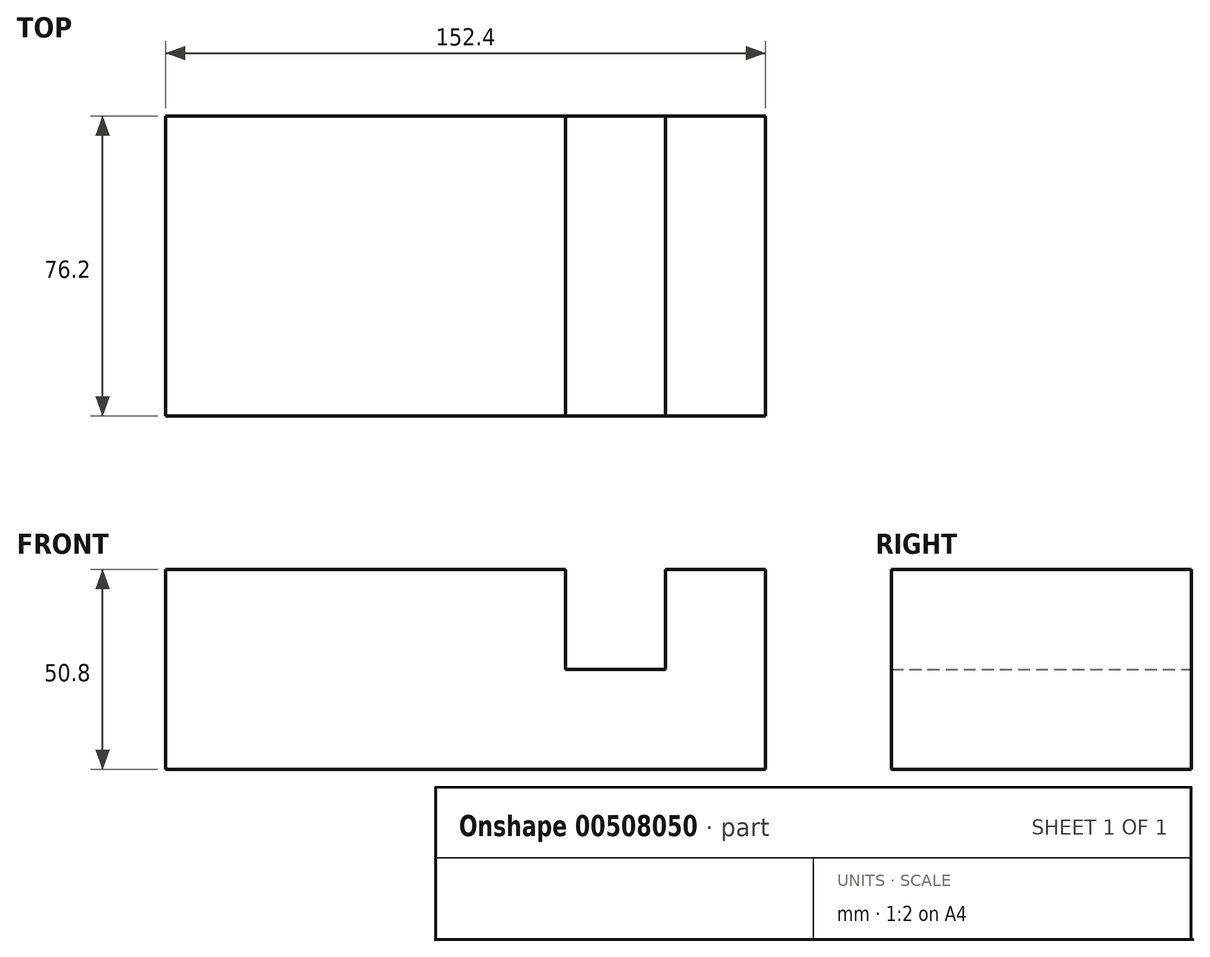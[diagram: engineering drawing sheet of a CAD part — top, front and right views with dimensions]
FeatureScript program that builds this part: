
annotation { "Feature Type Name" : "Feature", "Feature Type Description" : "" }
export const myFeature = defineFeature(function(context is Context, id is Id, definition is map)
    precondition{}
    {
        {
            var Q0;
            Q0=qCreatedBy(makeId("Front.planeOp"),FACE);
            var sketch = newSketch(context, id + "F0", { "sketchPlane" : qUnion([Q0])});
            skLineSegment(sketch, "E0", {"start": v(67.04, 43.43) * mm, "end": v(92.44, 43.43) * mm});
            skLineSegment(sketch, "E1", {"start": v(92.44, 43.43) * mm, "end": v(92.44, -7.37) * mm});
            skLineSegment(sketch, "E2", {"start": v(67.04, 43.43) * mm, "end": v(67.04, 18.03) * mm});
            skLineSegment(sketch, "E3", {"start": v(67.04, 18.03) * mm, "end": v(41.64, 18.03) * mm});
            skLineSegment(sketch, "E4", {"start": v(41.64, 18.03) * mm, "end": v(41.64, 43.43) * mm});
            skLineSegment(sketch, "E5", {"start": v(41.64, 43.43) * mm, "end": v(-59.96, 43.43) * mm});
            skLineSegment(sketch, "E6", {"start": v(-59.96, 43.43) * mm, "end": v(-59.96, -7.37) * mm});
            skLineSegment(sketch, "E7", {"start": v(-59.96, -7.37) * mm, "end": v(92.44, -7.37) * mm});
            skSolve(sketch);
        }
        {
            var Q0;
            Q0=makeQuery(id+"F0.imprint","IMPRINT",FACE,{"disambiguationData":[TD([[makeQuery(id+"F0.imprint","IMPRINT",EDGE,{"derivedFrom":sQuery(id+"F0.wireOp",EDGE,"E0")}),-1.0]])]});
            extrude(context, id + "F1", {"entities" : qUnion([Q0]), "depth" : 76.2 * mm});
        }
    });
